# Revit family: AV-04FD
name_source: partatom
category: Устройства связи
units: mm (PartAtom-declared; Revit-internal decimal feet)

## family parameters
Всегда вертикально = Нет
На основе рабочей плоскости = Да
Общий = Да
При загрузке вырезать с полостями = Нет
Размер круглого соединителя = Использовать диаметр
Сохранять ориентацию аннотаций = Нет
Тип детали = Нормальный
Точка принадлежности помещению = Нет

## types (1)
- AV-04FD
    ADSK_URL документации изделия = http://cdn.bas-ip.com
    ADSK_URL страницы изделия = https://www.bas-ip.ru
    ADSK_Версия Revit = Revit 2020
    ADSK_Единица измерения = шт
    ADSK_Завод-изготовитель = BAS-IP
    ADSK_Классификация нагрузок = Вызывная панель
    ADSK_Количество фаз = 1
    ADSK_Коэффициент мощности = 0.9
    ADSK_Марка = AV-04FD
    ADSK_Наименование = ВЫЗЫВНАЯ ПАНЕЛЬ AV-04FD
    ADSK_Наименование краткое = AV-04FD
    ADSK_Напряжение = 12 В
    ADSK_Номинальная мощность = 7 Вт
    ADSK_Полная мощность = 7 В·А
    ADSK_Размер_Длина = 190 мм
    ADSK_Размер_Толщина = 27 мм
    ADSK_Размер_Ширина = 95 мм
    BIM library = https://bimlib.ru
    URL = https://www.bas-ip.ru
    Аутентификация = Отдельный пароль на настройки, WEB–интерфейс, RTSP поток
    Выходное видео = 720p (1280x720), H.264 Main Profile
    Группа модели = Вызывная панель
    Дисплей = Нет
    Дополнительно = Подключение кнопки выхода, замка, SIP P2P,  открытое API
    Изготовитель = BAS-IP
    Изображение типоразмера = <Нет>
    Интеграция со СКУД = Не имеет выход Wiegand
    Интерфейс = Мультиязычный WEB–интерфейс
    Камера = 1/4”
    Класс степени защиты = IP65
    Кнопки быстрого вызова = 1 механическая кнопка вызова
    Корпус = Металл
    Материал корпуса = Материал серый
    Минимальная освещенность = 0,01 LuX
    Ночная подсветка = 6 светодиодов
    Описание = BAS-IP AV-04FD - данная индивидуальная вызывная панель сильно отличается в лучшую сторону по дизайну и характеристикам от обычных панелей, установленных в домах и квартирах. Благодаря степени защиты IP65, панель можно без проблем устанавливать на улице, не боясь сильного дождя и прочих “радостей” природы.
    Открытие замка = С монитора, через приложение BAS-IP Intercom
    Отметка по умолчанию = 0 мм
    Питание = + 12 Вольт, PoE
    Поддерживаемые аудиокодеки = G.711u
    Потребление питания = 6,5 Вт, в режиме ожидания – 3,6 Вт
    Размер панели с накладным кронштейном = 95х190х27 мм
    Размер под установку = 85х180х45 мм
    Разрешение камеры = 1.0 Мп
    Режим разговора = Двухсторонний
    Температурный режим = -40 ... +65 °С
    Тип панели = Индивидуальная
    Тип установки = Врезной
    Угол обзора = По горизонтали 110°, по вертикали 60°
    Цветовое решение = Серебро
